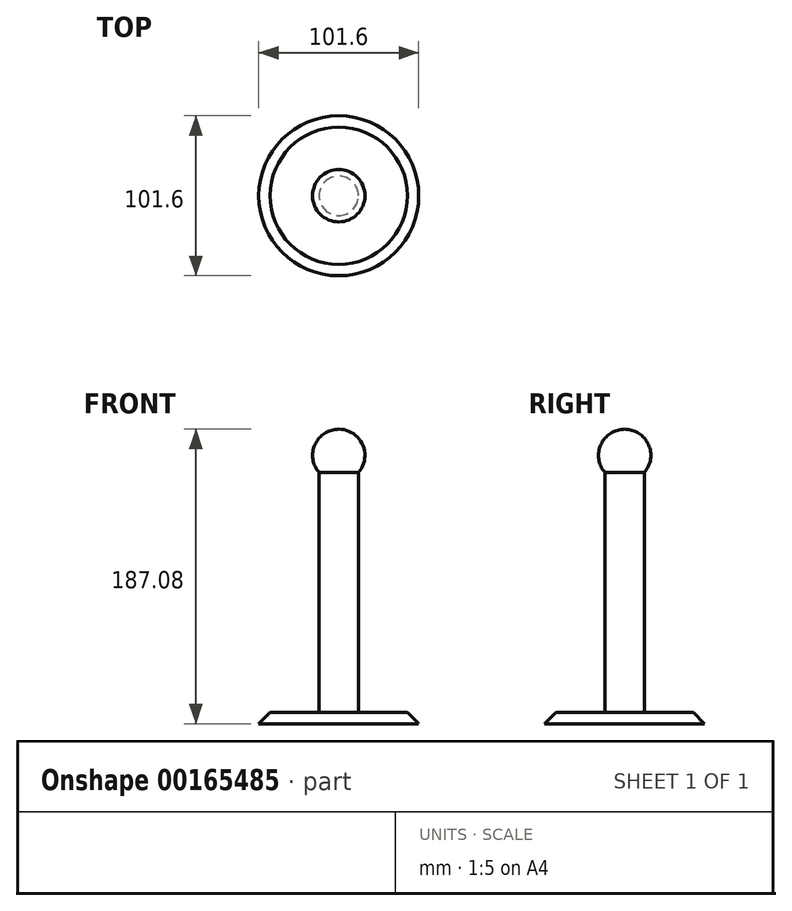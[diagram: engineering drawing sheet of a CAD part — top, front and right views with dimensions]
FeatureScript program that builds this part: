
annotation { "Feature Type Name" : "Feature", "Feature Type Description" : "" }
export const myFeature = defineFeature(function(context is Context, id is Id, definition is map)
    precondition{}
    {
        {
            var Q0;
            Q0=qCreatedBy(makeId("Front.planeOp"),FACE);
            var sketch = newSketch(context, id + "F0", { "sketchPlane" : qUnion([Q0])});
            skLineSegment(sketch, "E0", {"start": v(0, 0) * mm, "end": v(50.8, 0) * mm});
            skLineSegment(sketch, "E1", {"start": v(50.8, 0) * mm, "end": v(43.62, 7.18) * mm});
            skLineSegment(sketch, "E2", {"start": v(43.62, 7.18) * mm, "end": v(12.54, 7.18) * mm});
            skLineSegment(sketch, "E3", {"start": v(12.54, 7.18) * mm, "end": v(12.54, 159.58) * mm});
            skLineSegment(sketch, "E4", {"start": v(0, -46) * mm, "end": v(0, 171.92) * mm, "construction": true});
            skArc(sketch, "E5", {"start": v(12.54, 159.58) * mm, "mid": v(15.1, 177.36) * mm, "end": v(0, 187.08) * mm});
            skPoint(sketch, "E6.orphan", {"position": v(12.54, 170.47) * mm});
            skLineSegment(sketch, "E7", {"start": v(0, 187.08) * mm, "end": v(0, 0) * mm});
            skSolve(sketch);
        }
        {
            var Q0;
            Q0=makeQuery(id+"F0.imprint","IMPRINT",FACE,{"disambiguationData":[TD([[makeQuery(id+"F0.imprint","IMPRINT",EDGE,{"derivedFrom":sQuery(id+"F0.wireOp",EDGE,"E0")}),1.0]])]});
            var Q1;
            Q1=sQuery(id+"F0.wireOp",EDGE,"E7");
            revolve(context, id + "F1", {"entities" : qUnion([Q0]), "axis" : qUnion([Q1]), "revolveType" : RevolveType.FULL});
        }
    });
